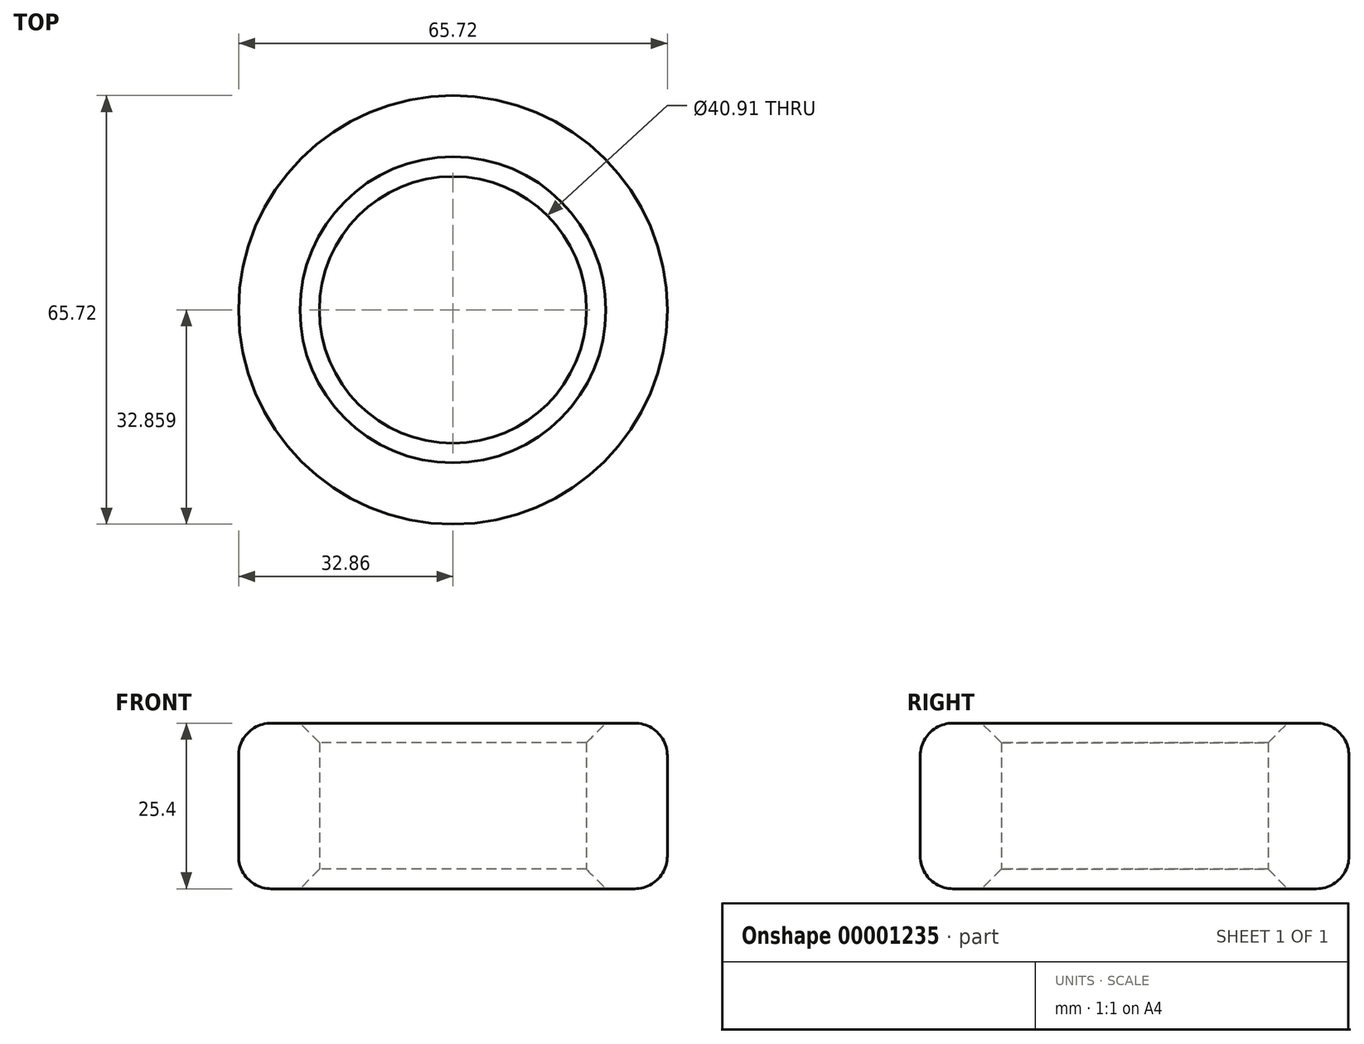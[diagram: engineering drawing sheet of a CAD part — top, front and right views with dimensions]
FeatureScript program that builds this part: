
annotation { "Feature Type Name" : "Feature", "Feature Type Description" : "" }
export const myFeature = defineFeature(function(context is Context, id is Id, definition is map)
    precondition{}
    {
        {
            var Q0;
            Q0=qCreatedBy(makeId("Top.planeOp"),FACE);
            var sketch = newSketch(context, id + "F0", { "sketchPlane" : qUnion([Q0])});
            skCircle(sketch, "E0", {"center": v(0, 2.76) * mm, "radius": 32.86 * mm});
            skCircle(sketch, "E1", {"center": v(0, 2.76) * mm, "radius": 20.46 * mm});
            skSolve(sketch);
        }
        {
            var Q0;
            Q0=makeQuery(id+"F0.imprint","IMPRINT",FACE,{"disambiguationData":[TD([[makeQuery(id+"F0.imprint","IMPRINT",EDGE,{"derivedFrom":sQuery(id+"F0.wireOp",EDGE,"E0")}),1.0]])]});
            extrude(context, id + "F1", {"entities" : qUnion([Q0]), "depth" : 25.4 * mm});
        }
        {
            var Q0;
            Q0=makeQuery(id+"F1.opExtrude","CAP_EDGE",EDGE,{"disambiguationData":[OSD([sQuery(id+"F0.wireOp",EDGE,"E0")])],"isStart":true});
            fillet(context, id + "F2", {"entities" : qUnion([Q0]), "radius" : 5 * mm, "tangentPropagation" : true, "allowEdgeOverflow" : false});
        }
        {
            var Q0;
            Q0=makeQuery(id+"F1.opExtrude","CAP_EDGE",EDGE,{"disambiguationData":[OSD([sQuery(id+"F0.wireOp",EDGE,"E0")])],"isStart":false});
            fillet(context, id + "F3", {"entities" : qUnion([Q0]), "radius" : 5 * mm, "tangentPropagation" : true, "allowEdgeOverflow" : false});
        }
        {
            var Q0;
            Q0=makeQuery(id+"F1.opExtrude","CAP_EDGE",EDGE,{"disambiguationData":[OSD([sQuery(id+"F0.wireOp",EDGE,"E1")])],"isStart":false});
            chamfer(context, id + "F4", {"entities" : qUnion([Q0]), "width" : 3 * mm, "tangentPropagation" : true});
        }
        {
            var Q0;
            Q0=makeQuery(id+"F1.opExtrude","CAP_EDGE",EDGE,{"disambiguationData":[OSD([sQuery(id+"F0.wireOp",EDGE,"E1")])],"isStart":true});
            chamfer(context, id + "F5", {"entities" : qUnion([Q0]), "width" : 3 * mm, "tangentPropagation" : true});
        }
    });
